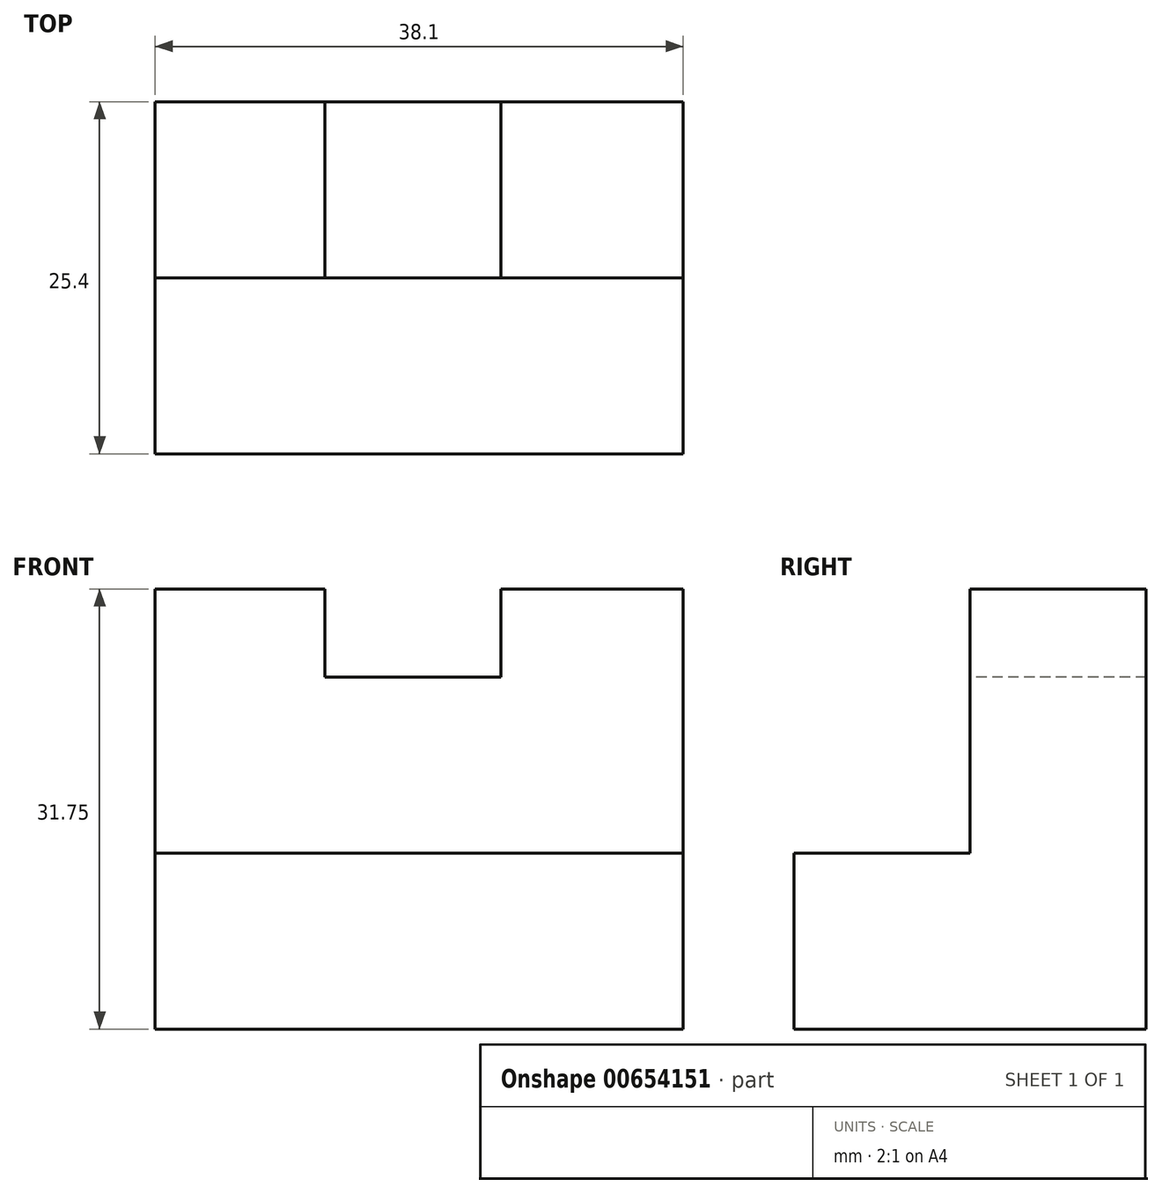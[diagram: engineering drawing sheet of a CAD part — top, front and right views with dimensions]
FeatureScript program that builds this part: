
annotation { "Feature Type Name" : "Feature", "Feature Type Description" : "" }
export const myFeature = defineFeature(function(context is Context, id is Id, definition is map)
    precondition{}
    {
        {
            var Q0;
            Q0=qCreatedBy(makeId("Right.planeOp"),FACE);
            var sketch = newSketch(context, id + "F0", { "sketchPlane" : qUnion([Q0])});
            skLineSegment(sketch, "E0", {"start": v(31.5, 42.7) * mm, "end": v(31.5, 10.95) * mm});
            skLineSegment(sketch, "E1", {"start": v(31.5, 10.95) * mm, "end": v(6.1, 10.95) * mm});
            skLineSegment(sketch, "E2", {"start": v(6.1, 10.95) * mm, "end": v(6.1, 23.65) * mm});
            skLineSegment(sketch, "E3", {"start": v(6.1, 23.65) * mm, "end": v(18.8, 23.65) * mm});
            skLineSegment(sketch, "E4", {"start": v(18.8, 23.65) * mm, "end": v(18.8, 42.7) * mm});
            skLineSegment(sketch, "E5", {"start": v(18.8, 42.7) * mm, "end": v(31.5, 42.7) * mm});
            skSolve(sketch);
        }
        {
            var Q0;
            Q0=makeQuery(id+"F0.imprint","IMPRINT",FACE,{"disambiguationData":[TD([[makeQuery(id+"F0.imprint","IMPRINT",EDGE,{"derivedFrom":sQuery(id+"F0.wireOp",EDGE,"E0")}),-1.0]])]});
            extrude(context, id + "F1", {"entities" : qUnion([Q0]), "depth" : 38.1 * mm, "offsetDistance" : 25.4 * mm});
        }
        {
            var Q0;
            Q0=makeQuery(id+"F1.opExtrude","SWEPT_FACE",FACE,{"disambiguationData":[OSD([sQuery(id+"F0.wireOp",EDGE,"E5")])]});
            var sketch = newSketch(context, id + "F2", { "sketchPlane" : qUnion([Q0])});
            skLineSegment(sketch, "E6", {"start": v(24.94, 31.5) * mm, "end": v(24.94, 18.8) * mm});
            skPoint(sketch, "E6.endSnap0", {"position": v(19.05, 18.8) * mm});
            skLineSegment(sketch, "E7", {"start": v(24.94, 18.8) * mm, "end": v(12.24, 18.8) * mm});
            skLineSegment(sketch, "E8", {"start": v(12.24, 18.8) * mm, "end": v(12.24, 31.5) * mm});
            skLineSegment(sketch, "E9", {"start": v(12.24, 31.5) * mm, "end": v(24.94, 31.5) * mm});
            skSolve(sketch);
        }
        {
            var Q0;
            Q0=makeQuery(id+"F2.imprint","IMPRINT",FACE,{"disambiguationData":[TD([[makeQuery(id+"F2.imprint","IMPRINT",EDGE,{"derivedFrom":sQuery(id+"F2.wireOp",EDGE,"E6")}),-1.0]])]});
            extrude(context, id + "F3", {"entities" : qUnion([Q0]), "operationType" : NewBodyOperationType.REMOVE, "oppositeDirection" : true, "depth" : 6.35 * mm, "offsetDistance" : 25.4 * mm});
        }
    });
